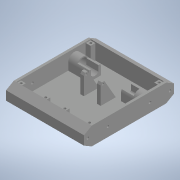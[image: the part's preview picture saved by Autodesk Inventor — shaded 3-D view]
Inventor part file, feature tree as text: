
AUTODESK INVENTOR PART (.ipt)
format: ipt  version: 2020 (Build 240168000, 168)  size: 399,360 bytes
history: native  units: in
note: dims shown in document units (in); Inventor stores cm internally (conversion verified against a paired STEP export)
features: projected_geometry x13, extrude x11, sketch x11, mirror x4, plane x1
ambient origin geometry x8: Origin, YZ Plane, XZ Plane, XY Plane, X Axis, Y Axis, Z Axis, Center Point
bodies: Solid1 (feature_tree)
feature tree (40):
  extrude  "Extrusion1"  Depth=5.9055in
  extrude  "Extrusion2"  TaperAngle=0.0deg  [1 undecoded]
  extrude  "Extrusion3"  Depth=1.063in
  extrude  "Extrusion4"  Depth=0.315in
  extrude  "Extrusion5"  TaperAngle=0.0deg  [1 undecoded]
  extrude  "Extrusion6"  Depth=0.5906in
  mirror  "Mirror1"
  extrude  "Extrusion7"  Depth=0.0787in
  mirror  "Mirror2"
  extrude  "Extrusion8"  Depth=0.5512in
  mirror  "Mirror3"
  plane  "Work Plane1"
  extrude  "Extrusion9"  Depth=0.7874in TaperAngle=0.0deg
  mirror  "Mirror4"
  extrude  "Extrusion10"  Depth=6.063in TaperAngle=0.0deg
  extrude  "Extrusion11"  Depth=0.1575in
  sketch  "Sketch1"  dims[d0=1.1811in d1=5.9055in]
  sketch  "Sketch2"  dims[d2=5.1181in d3=0.0in]
  projected_geometry  "Projected Loop1"
  sketch  "Sketch3"  dims[d4=0.1575in d5=1.063in]
  projected_geometry  "Projected Loop2"
  projected_geometry  "Projected Loop3"
  sketch  "Sketch4"  dims[d6=0.0in d8=0.315in]
  sketch  "Sketch5"  dims[d10=0.993in d11=0.0in]
  projected_geometry  "Projected Loop4"
  sketch  "Sketch6"  dims[d12=0.6496in d13=0.5906in]
  sketch  "Sketch7"  dims[d14=1.5748in d15=0.0787in]
  sketch  "Sketch9"  dims[d16=0.5512in d17=0.0in d18=0.6102in]
  sketch  "Sketch10"  dims[d19=0.4803in d20=0.7874in d21=0.0in]
  sketch  "Sketch12"  dims[d22=0.1654in d23=6.063in d24=0.0in]
  projected_geometry  "Projected Loop6"
  projected_geometry  "Projected Loop7"
  projected_geometry  "Projected Loop8"
  sketch  "Sketch13"  dims[d25=0.5114in d26=0.1575in d27=1.5748in d28=0.0in d29=0.0in d30=0.1575in d31=0.2756in d32=0.0in d33=0.4331in d34=0.122in d38=2.7559in d40=0.061in d41=0.0909in d42=0.2362in d43=0.0in d44=60.0deg d45=0.0787in d46=0.315in d48=0.993in d49=0.0in d51=0.1575in d52=0.1575in d53=0.2756in d54=0.0in d55=0.4724in]
  projected_geometry  "Projected Loop9"
  projected_geometry  "Projected Loop10"
  projected_geometry  "Projected Loop11"
  projected_geometry  "Projected Loop12"
  projected_geometry  "Projected Loop13"
  projected_geometry  "Projected Loop14"
note: 2 required parameter values undecoded (feature->parameter linkage not recoverable at this tier; creation-order binding heuristic only, values carry confidence <= 0.55)
